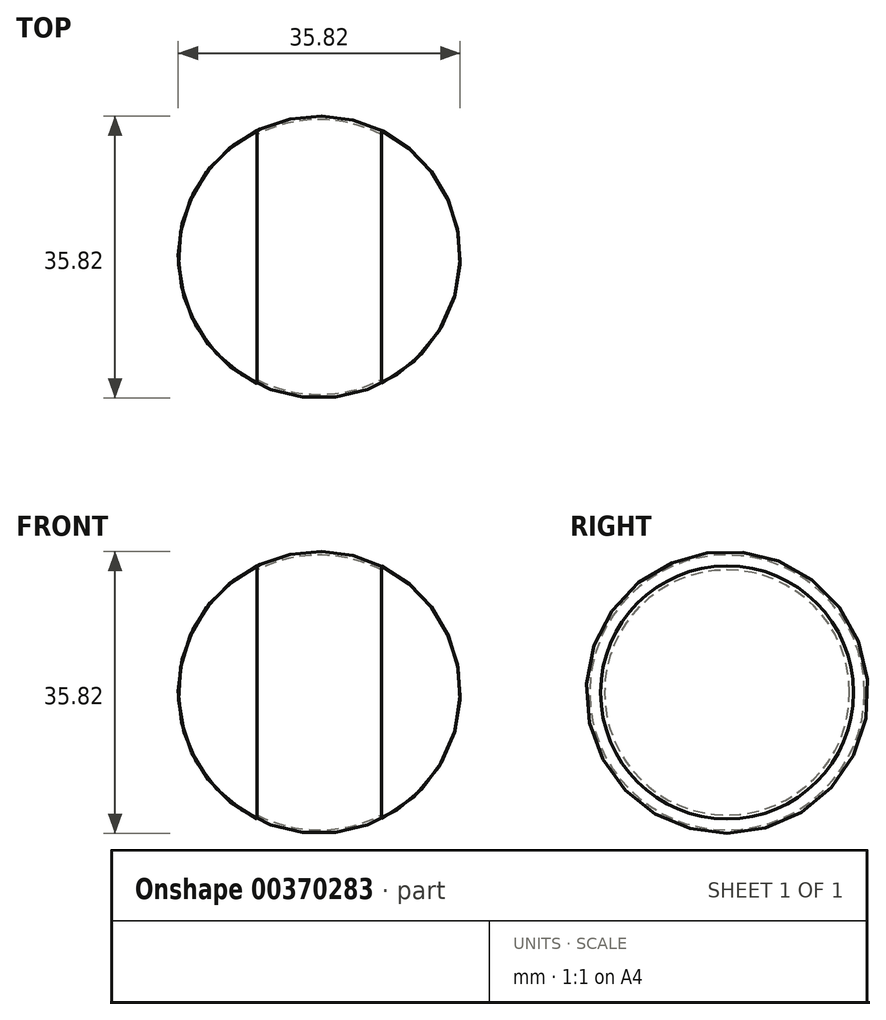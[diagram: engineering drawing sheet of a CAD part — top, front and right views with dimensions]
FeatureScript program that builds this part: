
annotation { "Feature Type Name" : "Feature", "Feature Type Description" : "" }
export const myFeature = defineFeature(function(context is Context, id is Id, definition is map)
    precondition{}
    {
        {
            var Q0;
            Q0=qCreatedBy(makeId("Front.planeOp"),FACE);
            var sketch = newSketch(context, id + "F0", { "sketchPlane" : qUnion([Q0])});
            skArc(sketch, "E0", {"start": v(7.91, 15.57) * mm, "mid": v(0, 17.46) * mm, "end": v(-7.9, 15.57) * mm});
            skLineSegment(sketch, "E1", {"start": v(-7.9, 15.57) * mm, "end": v(-7.9, 16.07) * mm, "construction": true});
            skLineSegment(sketch, "E2", {"start": v(7.72, 15.66) * mm, "end": v(7.9, 16.07) * mm, "construction": true});
            skArc(sketch, "E3", {"start": v(7.9, 16.07) * mm, "mid": v(0, 17.91) * mm, "end": v(-7.91, 16.07) * mm});
            skLineSegment(sketch, "E4", {"start": v(-7.9, 16.07) * mm, "end": v(-7.9, 15.57) * mm});
            skLineSegment(sketch, "E5", {"start": v(7.91, 16.07) * mm, "end": v(7.91, 15.57) * mm});
            skLineSegment(sketch, "E6", {"start": v(0, 0) * mm, "end": v(0, 17.46) * mm, "construction": true});
            skLineSegment(sketch, "E7", {"start": v(0, 17.46) * mm, "end": v(0, 17.91) * mm, "construction": true});
            skSolve(sketch);
        }
        {
            var Q0;
            Q0=qCreatedBy(makeId("Front.planeOp"),FACE);
            var sketch = newSketch(context, id + "F1", { "sketchPlane" : qUnion([Q0])});
            skLineSegment(sketch, "E8", {"start": v(-8.17, 0) * mm, "end": v(8.42, 0) * mm});
            skSolve(sketch);
        }
        {
            var Q0;
            Q0 = qSketchRegion(id + "F0", true);
            var Q1;
            Q1=sQuery(id+"F1.wireOp",EDGE,"E8");
            revolve(context, id + "F2", {"entities" : qUnion([Q0]), "axis" : qUnion([Q1]), "revolveType" : RevolveType.FULL});
        }
    });
